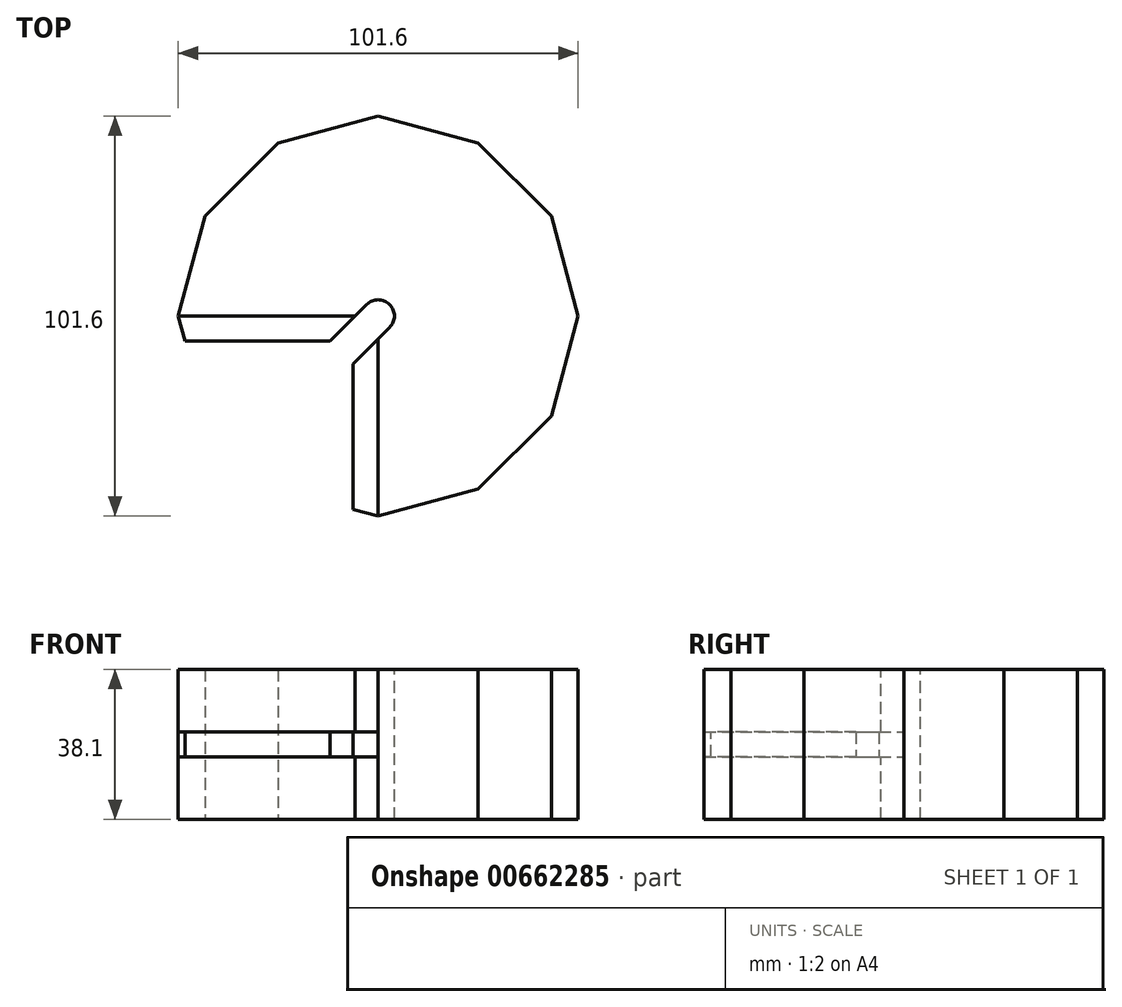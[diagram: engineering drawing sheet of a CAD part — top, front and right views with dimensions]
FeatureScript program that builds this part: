
annotation { "Feature Type Name" : "Feature", "Feature Type Description" : "" }
export const myFeature = defineFeature(function(context is Context, id is Id, definition is map)
    precondition{}
    {
        {
            var Q0;
            Q0=qCreatedBy(makeId("Top.planeOp"),FACE);
            var sketch = newSketch(context, id + "F0", { "sketchPlane" : qUnion([Q0])});
            skArc(sketch, "E0.cCircle", {"start": v(0, -50.8) * mm, "mid": v(35.92, 35.92) * mm, "end": v(-50.8, 0) * mm, "construction": true});
            skLineSegment(sketch, "E0.0", {"start": v(50.8, 0) * mm, "end": v(44, -25.4) * mm});
            skLineSegment(sketch, "E0.1", {"start": v(44, -25.4) * mm, "end": v(25.4, -44) * mm});
            skLineSegment(sketch, "E0.2", {"start": v(25.4, -44) * mm, "end": v(0, -50.8) * mm});
            skLineSegment(sketch, "E0.6", {"start": v(-50.8, 0) * mm, "end": v(-44, 25.4) * mm});
            skLineSegment(sketch, "E0.7", {"start": v(-44, 25.4) * mm, "end": v(-25.4, 44) * mm});
            skLineSegment(sketch, "E0.8", {"start": v(-25.4, 44) * mm, "end": v(0, 50.8) * mm});
            skLineSegment(sketch, "E0.9", {"start": v(0, 50.8) * mm, "end": v(25.4, 44) * mm});
            skLineSegment(sketch, "E0.10", {"start": v(25.4, 44) * mm, "end": v(44, 25.4) * mm});
            skLineSegment(sketch, "E0.11", {"start": v(44, 25.4) * mm, "end": v(50.8, 0) * mm});
            skLineSegment(sketch, "E1", {"start": v(-50.8, 0) * mm, "end": v(0, 0) * mm});
            skLineSegment(sketch, "E2", {"start": v(0, 0) * mm, "end": v(0, -50.8) * mm});
            skSolve(sketch);
        }
        {
            var Q0;
            Q0 = qSketchRegion(id + "F0", true);
            extrude(context, id + "F1", {"entities" : qUnion([Q0]), "depth" : 38.1 * mm, "offsetDistance" : 25.4 * mm});
        }
        {
            var Q0;
            Q0=makeQuery(id+"F1.opExtrude","SWEPT_FACE",FACE,{"disambiguationData":[OSD([sQuery(id+"F0.wireOp",EDGE,"E1")])]});
            var sketch = newSketch(context, id + "F2", { "sketchPlane" : qUnion([Q0])});
            skPoint(sketch, "E3", {"position": v(-50.8, 19.05) * mm});
            skPoint(sketch, "E4", {"position": v(0, 19.05) * mm});
            skLineSegment(sketch, "E5", {"start": v(-50.8, 19.05) * mm, "end": v(0, 19.05) * mm});
            skLineSegment(sketch, "E6.bottom", {"start": v(0, 15.88) * mm, "end": v(-50.8, 15.88) * mm});
            skLineSegment(sketch, "E6.top", {"start": v(0, 22.23) * mm, "end": v(-50.8, 22.23) * mm});
            skLineSegment(sketch, "E6.left", {"start": v(0, 15.88) * mm, "end": v(0, 22.23) * mm});
            skLineSegment(sketch, "E6.right", {"start": v(-50.8, 15.88) * mm, "end": v(-50.8, 22.23) * mm});
            skPoint(sketch, "E6.middle", {"position": v(-25.4, 19.05) * mm});
            skSolve(sketch);
        }
        {
            var Q0;
            Q0 = qSketchRegion(id + "F2", true);
            extrude(context, id + "F3", {"entities" : qUnion([Q0]), "operationType" : NewBodyOperationType.ADD, "depth" : 6.35 * mm, "offsetDistance" : 25.4 * mm});
        }
        {
            var Q0;
            Q0=makeQuery(id+"F3.opExtrude","SWEPT_FACE",FACE,{"disambiguationData":[OSD([sQuery(id+"F2.wireOp",EDGE,"E6.top")])]});
            var sketch = newSketch(context, id + "F4", { "sketchPlane" : qUnion([Q0])});
            skLineSegment(sketch, "E7", {"start": v(-50.8, 0) * mm, "end": v(-49.1, -6.35) * mm});
            skSolve(sketch);
        }
        {
            var Q0;
            {var subQ0=sQuery(id+"F4.wireOp",EDGE,"E7");Q0=makeQuery(id+"F4.imprint","IMPRINT",FACE,{"disambiguationData":[TD([[makeQuery(id+"F4.imprint","IMPRINT",EDGE,{"derivedFrom":subQ0}),-1.0]])]});}
            extrude(context, id + "F5", {"entities" : qUnion([Q0]), "operationType" : NewBodyOperationType.REMOVE, "oppositeDirection" : true, "depth" : 25.4 * mm, "offsetDistance" : 25.4 * mm});
        }
        {
            var Q0;
            Q0=makeQuery(id+"F1.opExtrude","SWEPT_FACE",FACE,{"disambiguationData":[OSD([sQuery(id+"F0.wireOp",EDGE,"E2")])]});
            var sketch = newSketch(context, id + "F6", { "sketchPlane" : qUnion([Q0])});
            skPoint(sketch, "E8.0", {"position": v(6.35, 22.23) * mm});
            skPoint(sketch, "E8.1", {"position": v(6.35, 15.88) * mm});
            skLineSegment(sketch, "E9", {"start": v(6.35, 22.23) * mm, "end": v(50.8, 22.23) * mm});
            skLineSegment(sketch, "E10", {"start": v(6.35, 15.88) * mm, "end": v(50.8, 15.88) * mm});
            skSolve(sketch);
        }
        {
            var Q0;
            {var subQ0=sQuery(id+"F6.wireOp",EDGE,"E9");Q0=makeQuery(id+"F6.imprint","IMPRINT",FACE,{"disambiguationData":[TD([[makeQuery(id+"F6.imprint","IMPRINT",EDGE,{"derivedFrom":subQ0}),-1.0]])]});}
            extrude(context, id + "F7", {"entities" : qUnion([Q0]), "operationType" : NewBodyOperationType.ADD, "depth" : 6.35 * mm, "offsetDistance" : 25.4 * mm});
        }
        {
            var Q0;
            Q0=makeQuery(id+"F7.boolean.opBoolean","MERGE",FACE,{"derivedFrom":[makeQuery(id+"F3.opExtrude","SWEPT_FACE",FACE,{"disambiguationData":[OSD([sQuery(id+"F2.wireOp",EDGE,"E6.top")])]}),makeQuery(id+"F7.opExtrude","SWEPT_FACE",FACE,{"disambiguationData":[OSD([sQuery(id+"F6.wireOp",EDGE,"E9")])]})]});
            var sketch = newSketch(context, id + "F8", { "sketchPlane" : qUnion([Q0])});
            skLineSegment(sketch, "E11", {"start": v(0, -50.8) * mm, "end": v(-6.35, -49.1) * mm});
            skSolve(sketch);
        }
        {
            var Q0;
            {var subQ0=sQuery(id+"F8.wireOp",EDGE,"E11");Q0=makeQuery(id+"F8.imprint","IMPRINT",FACE,{"disambiguationData":[TD([[makeQuery(id+"F8.imprint","IMPRINT",EDGE,{"derivedFrom":subQ0}),1.0]])]});}
            extrude(context, id + "F9", {"entities" : qUnion([Q0]), "operationType" : NewBodyOperationType.REMOVE, "oppositeDirection" : true, "depth" : 25.4 * mm, "offsetDistance" : 25.4 * mm});
        }
        {
            var Q0;
            Q0=makeQuery(id+"F1.opExtrude","CAP_FACE",FACE,{"disambiguationData":[OSD([sQuery(id+"F0.wireOp",EDGE,"E0.0"),sQuery(id+"F0.wireOp",EDGE,"E0.1"),sQuery(id+"F0.wireOp",EDGE,"E0.2"),sQuery(id+"F0.wireOp",EDGE,"E0.6"),sQuery(id+"F0.wireOp",EDGE,"E0.7"),sQuery(id+"F0.wireOp",EDGE,"E0.8"),sQuery(id+"F0.wireOp",EDGE,"E0.9"),sQuery(id+"F0.wireOp",EDGE,"E0.10"),sQuery(id+"F0.wireOp",EDGE,"E0.11"),sQuery(id+"F0.wireOp",EDGE,"E1"),sQuery(id+"F0.wireOp",EDGE,"E2")])],"isStart":false});
            var sketch = newSketch(context, id + "F10", { "sketchPlane" : qUnion([Q0])});
            skCircle(sketch, "E12", {"center": v(0, 0) * mm, "radius": 4.13 * mm});
            skSolve(sketch);
        }
        {
            var Q0;
            Q0 = qSketchRegion(id + "F10", true);
            extrude(context, id + "F11", {"entities" : qUnion([Q0]), "operationType" : NewBodyOperationType.REMOVE, "oppositeDirection" : true, "depth" : 127 * mm, "offsetDistance" : 25.4 * mm});
        }
        {
            var Q0;
            Q0=makeQuery(id+"F1.opExtrude","CAP_FACE",FACE,{"disambiguationData":[OSD([sQuery(id+"F0.wireOp",EDGE,"E0.0"),sQuery(id+"F0.wireOp",EDGE,"E0.1"),sQuery(id+"F0.wireOp",EDGE,"E0.2"),sQuery(id+"F0.wireOp",EDGE,"E0.6"),sQuery(id+"F0.wireOp",EDGE,"E0.7"),sQuery(id+"F0.wireOp",EDGE,"E0.8"),sQuery(id+"F0.wireOp",EDGE,"E0.9"),sQuery(id+"F0.wireOp",EDGE,"E0.10"),sQuery(id+"F0.wireOp",EDGE,"E0.11"),sQuery(id+"F0.wireOp",EDGE,"E1"),sQuery(id+"F0.wireOp",EDGE,"E2")])],"isStart":false});
            var sketch = newSketch(context, id + "F12", { "sketchPlane" : qUnion([Q0])});
            skLineSegment(sketch, "E13", {"start": v(0, 0) * mm, "end": v(-34.7, 34.7) * mm, "construction": true});
            skLineSegment(sketch, "E14", {"start": v(-34.7, 34.7) * mm, "end": v(34.7, -34.7) * mm, "construction": true});
            skLineSegment(sketch, "E15", {"start": v(-2.92, 2.92) * mm, "end": v(-18.8, -12.96) * mm});
            skLineSegment(sketch, "E16", {"start": v(2.92, -2.92) * mm, "end": v(-12.96, -18.8) * mm});
            skLineSegment(sketch, "E17", {"start": v(-12.96, -18.8) * mm, "end": v(-18.8, -12.96) * mm});
            skSolve(sketch);
        }
        {
            var Q0;
            {var subQ5=sQuery(id+"F12.wireOp",EDGE,"E17");Q0=makeQuery(id+"F12.imprint","IMPRINT",FACE,{"disambiguationData":[TD([[makeQuery(id+"F12.imprint","IMPRINT",EDGE,{"derivedFrom":subQ5}),-1.0]])]});}
            var Q1;
            {var subQ0=sQuery(id+"F12.wireOp",EDGE,"E15");var subQ1=makeQuery(id+"F11.boolean.opBoolean","COPY",EDGE,{"derivedFrom":makeQuery(id+"F11.opExtrude","CAP_EDGE",EDGE,{"disambiguationData":[OSD([sQuery(id+"F10.wireOp",EDGE,"E12")])],"isStart":true})});var subQ2=makeQuery(id+"F12.imprint","INTERSECT",VERTEX,{"derivedFrom":[subQ1,subQ0]});Q1=makeQuery(id+"F12.imprint","IMPRINT",FACE,{"disambiguationData":[TD([[makeQuery(id+"F12.imprint","IMPRINT",EDGE,{"disambiguationData":[TD([[subQ2,-1.0]])],"derivedFrom":subQ0}),1.0]])]});}
            var Q2;
            {var subQ0=sQuery(id+"F12.wireOp",EDGE,"E16");var subQ1=makeQuery(id+"F11.boolean.opBoolean","COPY",EDGE,{"derivedFrom":makeQuery(id+"F11.opExtrude","CAP_EDGE",EDGE,{"disambiguationData":[OSD([sQuery(id+"F10.wireOp",EDGE,"E12")])],"isStart":true})});var subQ2=makeQuery(id+"F12.imprint","INTERSECT",VERTEX,{"derivedFrom":[subQ1,subQ0]});Q2=makeQuery(id+"F12.imprint","IMPRINT",FACE,{"disambiguationData":[TD([[makeQuery(id+"F12.imprint","IMPRINT",EDGE,{"disambiguationData":[TD([[subQ2,-1.0]])],"derivedFrom":subQ0}),-1.0]])]});}
            extrude(context, id + "F13", {"entities" : qUnion([Q0, Q1, Q2]), "operationType" : NewBodyOperationType.REMOVE, "oppositeDirection" : true, "depth" : 127 * mm, "offsetDistance" : 25.4 * mm});
        }
    });
